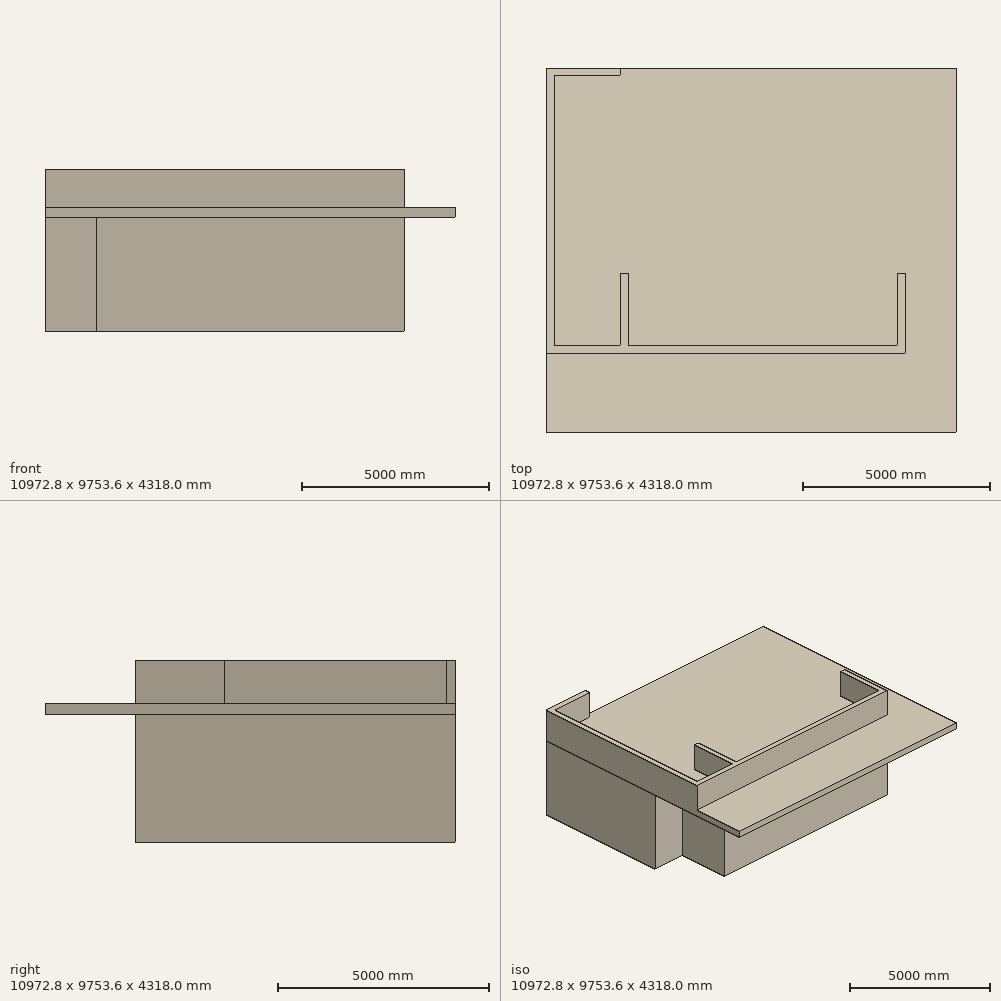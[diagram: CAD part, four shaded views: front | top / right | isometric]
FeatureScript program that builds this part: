
annotation { "Feature Type Name" : "Feature", "Feature Type Description" : "" }
export const myFeature = defineFeature(function(context is Context, id is Id, definition is map)
    precondition{}
    {
        {
            var Q0;
            Q0=qCreatedBy(makeId("Top.planeOp"),FACE);
            var sketch = newSketch(context, id + "F0", { "sketchPlane" : qUnion([Q0])});
            skLineSegment(sketch, "E0.bottom", {"start": v(-8229.6, 7620) * mm, "end": v(0, 7620) * mm});
            skLineSegment(sketch, "E0.top", {"start": v(-8229.6, 0) * mm, "end": v(0, 0) * mm});
            skLineSegment(sketch, "E0.left", {"start": v(-8229.6, 7620) * mm, "end": v(-8229.6, 0) * mm});
            skLineSegment(sketch, "E0.right", {"start": v(0, 7620) * mm, "end": v(0, 0) * mm});
            skLineSegment(sketch, "E1.bottom", {"start": v(-8077.2, 7467.6) * mm, "end": v(-152.4, 7467.6) * mm});
            skLineSegment(sketch, "E1.top", {"start": v(-8077.2, 152.4) * mm, "end": v(-152.4, 152.4) * mm});
            skLineSegment(sketch, "E1.left", {"start": v(-8077.2, 7467.6) * mm, "end": v(-8077.2, 152.4) * mm});
            skLineSegment(sketch, "E1.right", {"start": v(-152.4, 7467.6) * mm, "end": v(-152.4, 152.4) * mm});
            skSolve(sketch);
        }
        {
            var Q0;
            Q0 = qSketchRegion(id + "F0", true);
            extrude(context, id + "F1", {"entities" : qUnion([Q0]), "depth" : 3048 * mm});
        }
        {
            var Q0;
            Q0=qCreatedBy(makeId("Top.planeOp"),FACE);
            var sketch = newSketch(context, id + "F2", { "sketchPlane" : qUnion([Q0])});
            skLineSegment(sketch, "E2.bottom", {"start": v(-2934.46, 3909.43) * mm, "end": v(-1410.46, 3909.43) * mm});
            skLineSegment(sketch, "E2.top", {"start": v(-2934.46, 1166.23) * mm, "end": v(-1410.46, 1166.23) * mm});
            skLineSegment(sketch, "E2.left", {"start": v(-2934.46, 3909.43) * mm, "end": v(-2934.46, 1166.23) * mm});
            skLineSegment(sketch, "E2.right", {"start": v(-1410.46, 3909.43) * mm, "end": v(-1410.46, 1166.23) * mm});
            skSolve(sketch);
        }
        {
            var Q0;
            Q0 = qSketchRegion(id + "F2", true);
            extrude(context, id + "F3", {"entities" : qUnion([Q0]), "depth" : 1219.2 * mm});
        }
        {
            var Q0;
            Q0=qCreatedBy(makeId("Top.planeOp"),FACE);
            var sketch = newSketch(context, id + "F4", { "sketchPlane" : qUnion([Q0])});
            skLineSegment(sketch, "E3", {"start": v(-7377.5, 3939.47) * mm, "end": v(-5345.5, 3939.47) * mm});
            skLineSegment(sketch, "E4", {"start": v(-5345.5, 3939.47) * mm, "end": v(-5345.5, 637.47) * mm});
            skLineSegment(sketch, "E5", {"start": v(-5345.5, 637.47) * mm, "end": v(-7377.5, 637.47) * mm});
            skLineSegment(sketch, "E6", {"start": v(-6158.3, 3126.67) * mm, "end": v(-7377.5, 3126.67) * mm});
            skLineSegment(sketch, "E7", {"start": v(-7377.5, 3126.67) * mm, "end": v(-7377.5, 3939.47) * mm});
            skLineSegment(sketch, "E8", {"start": v(-6158.3, 3126.67) * mm, "end": v(-6158.3, 1450.27) * mm});
            skLineSegment(sketch, "E9", {"start": v(-6158.3, 1450.27) * mm, "end": v(-7377.5, 1450.27) * mm});
            skLineSegment(sketch, "E10", {"start": v(-7377.5, 1450.27) * mm, "end": v(-7377.5, 637.47) * mm});
            skSolve(sketch);
        }
        {
            var Q0;
            Q0 = qSketchRegion(id + "F4", true);
            extrude(context, id + "F5", {"entities" : qUnion([Q0]), "depth" : 914.4 * mm});
        }
        {
            var Q0;
            Q0=qCreatedBy(makeId("Top.planeOp"),FACE);
            var sketch = newSketch(context, id + "F6", { "sketchPlane" : qUnion([Q0])});
            skLineSegment(sketch, "E11.bottom", {"start": v(-8229.6, 7620) * mm, "end": v(-9601.2, 7620) * mm});
            skLineSegment(sketch, "E11.top", {"start": v(-8229.6, 2133.6) * mm, "end": v(-9601.2, 2133.6) * mm});
            skLineSegment(sketch, "E11.right", {"start": v(-9601.2, 7620) * mm, "end": v(-9601.2, 2133.6) * mm});
            skLineSegment(sketch, "E12.bottom", {"start": v(-9448.8, 7467.6) * mm, "end": v(-8229.6, 7467.6) * mm});
            skLineSegment(sketch, "E12.top", {"start": v(-9448.8, 2286) * mm, "end": v(-8229.6, 2286) * mm});
            skLineSegment(sketch, "E12.left", {"start": v(-9448.8, 7467.6) * mm, "end": v(-9448.8, 2286) * mm});
            skLineSegment(sketch, "E13", {"start": v(-8229.6, 7620) * mm, "end": v(-8229.6, 7467.6) * mm});
            skLineSegment(sketch, "E14", {"start": v(-8229.6, 2286) * mm, "end": v(-8229.6, 2133.6) * mm});
            skSolve(sketch);
        }
        {
            var Q0;
            Q0 = qSketchRegion(id + "F6", true);
            extrude(context, id + "F7", {"entities" : qUnion([Q0]), "operationType" : NewBodyOperationType.ADD, "depth" : 3048 * mm});
        }
        {
            var Q0;
            Q0=makeQuery(id+"F1.opExtrude","SWEPT_FACE",FACE,{"disambiguationData":[OSD([sQuery(id+"F0.wireOp",EDGE,"E1.left")])]});
            var sketch = newSketch(context, id + "F8", { "sketchPlane" : qUnion([Q0])});
            skLineSegment(sketch, "E15.bottom", {"start": v(2286, 0) * mm, "end": v(7467.6, 0) * mm});
            skLineSegment(sketch, "E15.top", {"start": v(2286, 3048) * mm, "end": v(7467.6, 3048) * mm});
            skLineSegment(sketch, "E15.left", {"start": v(2286, 0) * mm, "end": v(2286, 3048) * mm});
            skLineSegment(sketch, "E15.right", {"start": v(7467.6, 0) * mm, "end": v(7467.6, 3048) * mm});
            skSolve(sketch);
        }
        {
            var Q0;
            Q0 = qSketchRegion(id + "F8", true);
            extrude(context, id + "F9", {"entities" : qUnion([Q0]), "operationType" : NewBodyOperationType.REMOVE, "endBound" : BoundingType.UP_TO_NEXT, "oppositeDirection" : true, "depth" : 25.4 * mm});
        }
        {
            var Q0;
            Q0=makeQuery(id+"F7.boolean.opBoolean","MERGE",FACE,{"derivedFrom":[makeQuery(id+"F1.opExtrude","CAP_FACE",FACE,{"disambiguationData":[OSD([sQuery(id+"F0.wireOp",EDGE,"E0.bottom"),sQuery(id+"F0.wireOp",EDGE,"E0.top"),sQuery(id+"F0.wireOp",EDGE,"E0.left"),sQuery(id+"F0.wireOp",EDGE,"E0.right"),sQuery(id+"F0.wireOp",EDGE,"E1.bottom"),sQuery(id+"F0.wireOp",EDGE,"E1.top"),sQuery(id+"F0.wireOp",EDGE,"E1.left"),sQuery(id+"F0.wireOp",EDGE,"E1.right")])],"isStart":false}),makeQuery(id+"F7.opExtrude","CAP_FACE",FACE,{"disambiguationData":[OSD([sQuery(id+"F6.wireOp",EDGE,"E11.bottom"),sQuery(id+"F6.wireOp",EDGE,"E11.top"),sQuery(id+"F6.wireOp",EDGE,"E11.right"),sQuery(id+"F6.wireOp",EDGE,"E12.bottom"),sQuery(id+"F6.wireOp",EDGE,"E12.top"),sQuery(id+"F6.wireOp",EDGE,"E12.left"),sQuery(id+"F6.wireOp",EDGE,"E13"),sQuery(id+"F6.wireOp",EDGE,"E14")])],"isStart":false})]});
            var sketch = newSketch(context, id + "F10", { "sketchPlane" : qUnion([Q0])});
            skLineSegment(sketch, "E16", {"start": v(-6248.4, 7467.6) * mm, "end": v(-6248.4, 6502.4) * mm});
            skLineSegment(sketch, "E17", {"start": v(-6248.4, 6502.4) * mm, "end": v(-9448.8, 6502.4) * mm});
            skLineSegment(sketch, "E18", {"start": v(-9448.8, 6654.8) * mm, "end": v(-6400.8, 6654.8) * mm});
            skLineSegment(sketch, "E19", {"start": v(-6400.8, 6654.8) * mm, "end": v(-6400.8, 7467.6) * mm});
            skLineSegment(sketch, "E20", {"start": v(-6400.8, 7467.6) * mm, "end": v(-6248.4, 7467.6) * mm});
            skLineSegment(sketch, "E21", {"start": v(-9448.8, 6654.8) * mm, "end": v(-9448.8, 6502.4) * mm});
            skSolve(sketch);
        }
        {
            var Q0;
            Q0 = qSketchRegion(id + "F10", true);
            var Q1;
            Q1=makeQuery(id+"F7.boolean.opBoolean","MERGE",FACE,{"derivedFrom":[makeQuery(id+"F1.opExtrude","CAP_FACE",FACE,{"disambiguationData":[OSD([sQuery(id+"F0.wireOp",EDGE,"E0.bottom"),sQuery(id+"F0.wireOp",EDGE,"E0.top"),sQuery(id+"F0.wireOp",EDGE,"E0.left"),sQuery(id+"F0.wireOp",EDGE,"E0.right"),sQuery(id+"F0.wireOp",EDGE,"E1.bottom"),sQuery(id+"F0.wireOp",EDGE,"E1.top"),sQuery(id+"F0.wireOp",EDGE,"E1.left"),sQuery(id+"F0.wireOp",EDGE,"E1.right")])],"isStart":true}),makeQuery(id+"F7.opExtrude","CAP_FACE",FACE,{"disambiguationData":[OSD([sQuery(id+"F6.wireOp",EDGE,"E11.bottom"),sQuery(id+"F6.wireOp",EDGE,"E11.top"),sQuery(id+"F6.wireOp",EDGE,"E11.right"),sQuery(id+"F6.wireOp",EDGE,"E12.bottom"),sQuery(id+"F6.wireOp",EDGE,"E12.top"),sQuery(id+"F6.wireOp",EDGE,"E12.left"),sQuery(id+"F6.wireOp",EDGE,"E13"),sQuery(id+"F6.wireOp",EDGE,"E14")])],"isStart":true})]});
            extrude(context, id + "F11", {"entities" : qUnion([Q0]), "operationType" : NewBodyOperationType.ADD, "endBound" : BoundingType.UP_TO_SURFACE, "oppositeDirection" : true, "endBoundEntityFace" : qUnion([Q1]), "depth" : 25.4 * mm});
        }
        {
            var Q0;
            {var subQ0=sQuery(id+"F6.wireOp",EDGE,"E14");var subQ1=sQuery(id+"F6.wireOp",EDGE,"E13");var subQ2=sQuery(id+"F6.wireOp",EDGE,"E12.left");var subQ3=sQuery(id+"F6.wireOp",EDGE,"E12.top");var subQ4=sQuery(id+"F6.wireOp",EDGE,"E12.bottom");var subQ5=sQuery(id+"F6.wireOp",EDGE,"E11.right");var subQ6=sQuery(id+"F6.wireOp",EDGE,"E11.top");var subQ7=sQuery(id+"F6.wireOp",EDGE,"E11.bottom");var subQ8=sQuery(id+"F0.wireOp",EDGE,"E1.right");var subQ9=sQuery(id+"F0.wireOp",EDGE,"E1.left");var subQ10=sQuery(id+"F0.wireOp",EDGE,"E1.top");var subQ11=sQuery(id+"F0.wireOp",EDGE,"E1.bottom");var subQ12=sQuery(id+"F0.wireOp",EDGE,"E0.right");var subQ13=sQuery(id+"F0.wireOp",EDGE,"E0.left");var subQ14=sQuery(id+"F0.wireOp",EDGE,"E0.top");var subQ15=sQuery(id+"F0.wireOp",EDGE,"E0.bottom");Q0=makeQuery(id+"F11.boolean.opBoolean","MERGE",FACE,{"derivedFrom":[makeQuery(id+"F7.boolean.opBoolean","MERGE",FACE,{"derivedFrom":[makeQuery(id+"F1.opExtrude","CAP_FACE",FACE,{"disambiguationData":[OSD([subQ15,subQ14,subQ13,subQ12,subQ11,subQ10,subQ9,subQ8])],"isStart":true}),makeQuery(id+"F7.opExtrude","CAP_FACE",FACE,{"disambiguationData":[OSD([subQ7,subQ6,subQ5,subQ4,subQ3,subQ2,subQ1,subQ0])],"isStart":true})]}),makeQuery(id+"F11.opExtrude","CAP_FACE",FACE,{"disambiguationData":[OSD([subQ15,subQ14,subQ13,subQ12,subQ11,subQ10,subQ9,subQ8,subQ7,subQ6,subQ5,subQ4,subQ3,subQ2,subQ1,subQ0])],"isStart":false})]});}
            var sketch = newSketch(context, id + "F12", { "sketchPlane" : qUnion([Q0])});
            skLineSegment(sketch, "E22", {"start": v(-6248.4, -6502.4) * mm, "end": v(-6248.4, -5283.2) * mm});
            skLineSegment(sketch, "E23", {"start": v(-6248.4, -5283.2) * mm, "end": v(-8077.2, -5283.2) * mm});
            skLineSegment(sketch, "E24", {"start": v(-8229.6, -5435.6) * mm, "end": v(-6400.8, -5435.6) * mm});
            skLineSegment(sketch, "E25", {"start": v(-6400.8, -5435.6) * mm, "end": v(-6400.8, -6502.4) * mm});
            skLineSegment(sketch, "E26", {"start": v(-6400.8, -6502.4) * mm, "end": v(-6248.4, -6502.4) * mm});
            skLineSegment(sketch, "E27", {"start": v(-8229.6, -5435.6) * mm, "end": v(-8229.6, -3505.2) * mm});
            skLineSegment(sketch, "E28", {"start": v(-8229.6, -3505.2) * mm, "end": v(-8077.2, -3505.2) * mm});
            skLineSegment(sketch, "E29", {"start": v(-8077.2, -3505.2) * mm, "end": v(-8077.2, -5283.2) * mm});
            skSolve(sketch);
        }
        {
            var Q0;
            Q0 = qSketchRegion(id + "F12", true);
            var Q1;
            Q1=makeQuery(id+"F11.boolean.opBoolean","MERGE",FACE,{"derivedFrom":[makeQuery(id+"F7.boolean.opBoolean","MERGE",FACE,{"derivedFrom":[makeQuery(id+"F1.opExtrude","CAP_FACE",FACE,{"disambiguationData":[OSD([sQuery(id+"F0.wireOp",EDGE,"E0.bottom"),sQuery(id+"F0.wireOp",EDGE,"E0.top"),sQuery(id+"F0.wireOp",EDGE,"E0.left"),sQuery(id+"F0.wireOp",EDGE,"E0.right"),sQuery(id+"F0.wireOp",EDGE,"E1.bottom"),sQuery(id+"F0.wireOp",EDGE,"E1.top"),sQuery(id+"F0.wireOp",EDGE,"E1.left"),sQuery(id+"F0.wireOp",EDGE,"E1.right")])],"isStart":false}),makeQuery(id+"F7.opExtrude","CAP_FACE",FACE,{"disambiguationData":[OSD([sQuery(id+"F6.wireOp",EDGE,"E11.bottom"),sQuery(id+"F6.wireOp",EDGE,"E11.top"),sQuery(id+"F6.wireOp",EDGE,"E11.right"),sQuery(id+"F6.wireOp",EDGE,"E12.bottom"),sQuery(id+"F6.wireOp",EDGE,"E12.top"),sQuery(id+"F6.wireOp",EDGE,"E12.left"),sQuery(id+"F6.wireOp",EDGE,"E13"),sQuery(id+"F6.wireOp",EDGE,"E14")])],"isStart":false})]}),makeQuery(id+"F11.opExtrude","CAP_FACE",FACE,{"disambiguationData":[OSD([sQuery(id+"F10.wireOp",EDGE,"E16"),sQuery(id+"F10.wireOp",EDGE,"E17"),sQuery(id+"F10.wireOp",EDGE,"E18"),sQuery(id+"F10.wireOp",EDGE,"E19"),sQuery(id+"F10.wireOp",EDGE,"E20"),sQuery(id+"F10.wireOp",EDGE,"E21")])],"isStart":true})]});
            extrude(context, id + "F13", {"entities" : qUnion([Q0]), "operationType" : NewBodyOperationType.ADD, "oppositeDirection" : true, "endBoundEntityFace" : qUnion([Q1]), "depth" : 914.4 * mm});
        }
        {
            var Q0;
            Q0=makeQuery(id+"F1.opExtrude","SWEPT_FACE",FACE,{"disambiguationData":[OSD([sQuery(id+"F0.wireOp",EDGE,"E0.right")])]});
            var sketch = newSketch(context, id + "F14", { "sketchPlane" : qUnion([Q0])});
            skLineSegment(sketch, "E30.bottom", {"start": v(0, 3048) * mm, "end": v(7620, 3048) * mm});
            skLineSegment(sketch, "E30.top", {"start": v(0, 0) * mm, "end": v(7620, 0) * mm});
            skLineSegment(sketch, "E30.left", {"start": v(0, 3048) * mm, "end": v(0, 0) * mm});
            skLineSegment(sketch, "E30.right", {"start": v(7620, 3048) * mm, "end": v(7620, 0) * mm});
            skSolve(sketch);
        }
        {
            var Q0;
            Q0=makeQuery(id+"F11.boolean.opBoolean","MERGE",FACE,{"derivedFrom":[makeQuery(id+"F7.boolean.opBoolean","MERGE",FACE,{"derivedFrom":[makeQuery(id+"F1.opExtrude","CAP_FACE",FACE,{"disambiguationData":[OSD([sQuery(id+"F0.wireOp",EDGE,"E0.bottom"),sQuery(id+"F0.wireOp",EDGE,"E0.top"),sQuery(id+"F0.wireOp",EDGE,"E0.left"),sQuery(id+"F0.wireOp",EDGE,"E0.right"),sQuery(id+"F0.wireOp",EDGE,"E1.bottom"),sQuery(id+"F0.wireOp",EDGE,"E1.top"),sQuery(id+"F0.wireOp",EDGE,"E1.left"),sQuery(id+"F0.wireOp",EDGE,"E1.right")])],"isStart":false}),makeQuery(id+"F7.opExtrude","CAP_FACE",FACE,{"disambiguationData":[OSD([sQuery(id+"F6.wireOp",EDGE,"E11.bottom"),sQuery(id+"F6.wireOp",EDGE,"E11.top"),sQuery(id+"F6.wireOp",EDGE,"E11.right"),sQuery(id+"F6.wireOp",EDGE,"E12.bottom"),sQuery(id+"F6.wireOp",EDGE,"E12.top"),sQuery(id+"F6.wireOp",EDGE,"E12.left"),sQuery(id+"F6.wireOp",EDGE,"E13"),sQuery(id+"F6.wireOp",EDGE,"E14")])],"isStart":false})]}),makeQuery(id+"F11.opExtrude","CAP_FACE",FACE,{"disambiguationData":[OSD([sQuery(id+"F10.wireOp",EDGE,"E16"),sQuery(id+"F10.wireOp",EDGE,"E17"),sQuery(id+"F10.wireOp",EDGE,"E18"),sQuery(id+"F10.wireOp",EDGE,"E19"),sQuery(id+"F10.wireOp",EDGE,"E20"),sQuery(id+"F10.wireOp",EDGE,"E21")])],"isStart":true})]});
            var sketch = newSketch(context, id + "F15", { "sketchPlane" : qUnion([Q0])});
            skLineSegment(sketch, "E31.bottom", {"start": v(-9601.2, 7620) * mm, "end": v(0, 7620) * mm});
            skLineSegment(sketch, "E31.top", {"start": v(-9601.2, 0) * mm, "end": v(0, 0) * mm});
            skLineSegment(sketch, "E31.left", {"start": v(-9601.2, 7620) * mm, "end": v(-9601.2, 0) * mm});
            skLineSegment(sketch, "E31.right", {"start": v(0, 7620) * mm, "end": v(0, 0) * mm});
            skSolve(sketch);
        }
        {
            var Q0;
            Q0 = qSketchRegion(id + "F15", true);
            extrude(context, id + "F16", {"entities" : qUnion([Q0]), "depth" : 254 * mm});
        }
        {
            var Q0;
            Q0=makeQuery(id+"F16.opExtrude","CAP_FACE",FACE,{"disambiguationData":[OSD([sQuery(id+"F15.wireOp",EDGE,"E31.bottom"),sQuery(id+"F15.wireOp",EDGE,"E31.top"),sQuery(id+"F15.wireOp",EDGE,"E31.left"),sQuery(id+"F15.wireOp",EDGE,"E31.right")])],"isStart":false});
            var sketch = newSketch(context, id + "F17", { "sketchPlane" : qUnion([Q0])});
            skLineSegment(sketch, "E32", {"start": v(0, 2133.6) * mm, "end": v(0, 0) * mm});
            skLineSegment(sketch, "E33", {"start": v(0, 0) * mm, "end": v(-9601.2, 0) * mm});
            skLineSegment(sketch, "E34", {"start": v(-9601.2, 0) * mm, "end": v(-9601.2, 7620) * mm});
            skLineSegment(sketch, "E35", {"start": v(-9601.2, 7620) * mm, "end": v(-7620, 7620) * mm});
            skLineSegment(sketch, "E36", {"start": v(-7620, 7620) * mm, "end": v(-7620, 7416.8) * mm});
            skLineSegment(sketch, "E37", {"start": v(-7620, 7416.8) * mm, "end": v(-9398, 7416.8) * mm});
            skLineSegment(sketch, "E38", {"start": v(-9398, 7416.8) * mm, "end": v(-9398, 203.2) * mm});
            skLineSegment(sketch, "E39", {"start": v(-9398, 203.2) * mm, "end": v(-203.2, 203.2) * mm});
            skLineSegment(sketch, "E40", {"start": v(-203.2, 203.2) * mm, "end": v(-203.2, 2133.6) * mm});
            skLineSegment(sketch, "E41", {"start": v(-203.2, 2133.6) * mm, "end": v(0, 2133.6) * mm});
            skSolve(sketch);
        }
        {
            var Q0;
            Q0 = qSketchRegion(id + "F17", true);
            extrude(context, id + "F18", {"entities" : qUnion([Q0]), "operationType" : NewBodyOperationType.ADD, "depth" : 1016 * mm});
        }
        {
            var Q0;
            Q0=makeQuery(id+"F11.boolean.opBoolean","MERGE",FACE,{"derivedFrom":[makeQuery(id+"F7.boolean.opBoolean","MERGE",FACE,{"derivedFrom":[makeQuery(id+"F1.opExtrude","CAP_FACE",FACE,{"disambiguationData":[OSD([sQuery(id+"F0.wireOp",EDGE,"E0.bottom"),sQuery(id+"F0.wireOp",EDGE,"E0.top"),sQuery(id+"F0.wireOp",EDGE,"E0.left"),sQuery(id+"F0.wireOp",EDGE,"E0.right"),sQuery(id+"F0.wireOp",EDGE,"E1.bottom"),sQuery(id+"F0.wireOp",EDGE,"E1.top"),sQuery(id+"F0.wireOp",EDGE,"E1.left"),sQuery(id+"F0.wireOp",EDGE,"E1.right")])],"isStart":false}),makeQuery(id+"F7.opExtrude","CAP_FACE",FACE,{"disambiguationData":[OSD([sQuery(id+"F6.wireOp",EDGE,"E11.bottom"),sQuery(id+"F6.wireOp",EDGE,"E11.top"),sQuery(id+"F6.wireOp",EDGE,"E11.right"),sQuery(id+"F6.wireOp",EDGE,"E12.bottom"),sQuery(id+"F6.wireOp",EDGE,"E12.top"),sQuery(id+"F6.wireOp",EDGE,"E12.left"),sQuery(id+"F6.wireOp",EDGE,"E13"),sQuery(id+"F6.wireOp",EDGE,"E14")])],"isStart":false})]}),makeQuery(id+"F11.opExtrude","CAP_FACE",FACE,{"disambiguationData":[OSD([sQuery(id+"F10.wireOp",EDGE,"E16"),sQuery(id+"F10.wireOp",EDGE,"E17"),sQuery(id+"F10.wireOp",EDGE,"E18"),sQuery(id+"F10.wireOp",EDGE,"E19"),sQuery(id+"F10.wireOp",EDGE,"E20"),sQuery(id+"F10.wireOp",EDGE,"E21")])],"isStart":true})]});
            var sketch = newSketch(context, id + "F19", { "sketchPlane" : qUnion([Q0])});
            skLineSegment(sketch, "E42.bottom", {"start": v(-9601.2, 7620) * mm, "end": v(1371.6, 7620) * mm});
            skLineSegment(sketch, "E42.top", {"start": v(-9601.2, -2133.6) * mm, "end": v(1371.6, -2133.6) * mm});
            skLineSegment(sketch, "E42.left", {"start": v(-9601.2, 7620) * mm, "end": v(-9601.2, -2133.6) * mm});
            skLineSegment(sketch, "E42.right", {"start": v(1371.6, 7620) * mm, "end": v(1371.6, -2133.6) * mm});
            skSolve(sketch);
        }
        {
            var Q0;
            Q0 = qSketchRegion(id + "F19", true);
            extrude(context, id + "F20", {"entities" : qUnion([Q0]), "depth" : 254 * mm});
        }
        {
            var Q0;
            Q0=makeQuery(id+"F11.boolean.opBoolean","MERGE",FACE,{"derivedFrom":[makeQuery(id+"F7.boolean.opBoolean","MERGE",FACE,{"derivedFrom":[makeQuery(id+"F1.opExtrude","CAP_FACE",FACE,{"disambiguationData":[OSD([sQuery(id+"F0.wireOp",EDGE,"E0.bottom"),sQuery(id+"F0.wireOp",EDGE,"E0.top"),sQuery(id+"F0.wireOp",EDGE,"E0.left"),sQuery(id+"F0.wireOp",EDGE,"E0.right"),sQuery(id+"F0.wireOp",EDGE,"E1.bottom"),sQuery(id+"F0.wireOp",EDGE,"E1.top"),sQuery(id+"F0.wireOp",EDGE,"E1.left"),sQuery(id+"F0.wireOp",EDGE,"E1.right")])],"isStart":false}),makeQuery(id+"F7.opExtrude","CAP_FACE",FACE,{"disambiguationData":[OSD([sQuery(id+"F6.wireOp",EDGE,"E11.bottom"),sQuery(id+"F6.wireOp",EDGE,"E11.top"),sQuery(id+"F6.wireOp",EDGE,"E11.right"),sQuery(id+"F6.wireOp",EDGE,"E12.bottom"),sQuery(id+"F6.wireOp",EDGE,"E12.top"),sQuery(id+"F6.wireOp",EDGE,"E12.left"),sQuery(id+"F6.wireOp",EDGE,"E13"),sQuery(id+"F6.wireOp",EDGE,"E14")])],"isStart":false})]}),makeQuery(id+"F11.opExtrude","CAP_FACE",FACE,{"disambiguationData":[OSD([sQuery(id+"F10.wireOp",EDGE,"E16"),sQuery(id+"F10.wireOp",EDGE,"E17"),sQuery(id+"F10.wireOp",EDGE,"E18"),sQuery(id+"F10.wireOp",EDGE,"E19"),sQuery(id+"F10.wireOp",EDGE,"E20"),sQuery(id+"F10.wireOp",EDGE,"E21")])],"isStart":true})]});
            var sketch = newSketch(context, id + "F21", { "sketchPlane" : qUnion([Q0])});
            skLineSegment(sketch, "E43.bottom", {"start": v(-9601.2, 7620) * mm, "end": v(0, 7620) * mm});
            skLineSegment(sketch, "E43.top", {"start": v(-9601.2, 0) * mm, "end": v(0, 0) * mm});
            skLineSegment(sketch, "E43.left", {"start": v(-9601.2, 7620) * mm, "end": v(-9601.2, 0) * mm});
            skLineSegment(sketch, "E43.right", {"start": v(0, 7620) * mm, "end": v(0, 0) * mm});
            skSolve(sketch);
        }
        {
            var Q0;
            Q0 = qSketchRegion(id + "F21", true);
            extrude(context, id + "F22", {"entities" : qUnion([Q0]), "depth" : 254 * mm});
        }
        {
            var Q0;
            Q0=makeQuery(id+"F22.opExtrude","CAP_FACE",FACE,{"disambiguationData":[OSD([sQuery(id+"F21.wireOp",EDGE,"E43.bottom"),sQuery(id+"F21.wireOp",EDGE,"E43.top"),sQuery(id+"F21.wireOp",EDGE,"E43.left"),sQuery(id+"F21.wireOp",EDGE,"E43.right")])],"isStart":false});
            var sketch = newSketch(context, id + "F23", { "sketchPlane" : qUnion([Q0])});
            skLineSegment(sketch, "E44", {"start": v(0, 2133.6) * mm, "end": v(0, 0) * mm});
            skLineSegment(sketch, "E45", {"start": v(0, 0) * mm, "end": v(-7620, 0) * mm});
            skLineSegment(sketch, "E46", {"start": v(-7620, 0) * mm, "end": v(-7620, 2133.6) * mm});
            skLineSegment(sketch, "E47", {"start": v(-7620, 2133.6) * mm, "end": v(-7416.8, 2133.6) * mm});
            skLineSegment(sketch, "E48", {"start": v(-7416.8, 2133.6) * mm, "end": v(-7416.8, 203.2) * mm});
            skLineSegment(sketch, "E49", {"start": v(-7416.8, 203.2) * mm, "end": v(-203.2, 203.2) * mm});
            skLineSegment(sketch, "E50", {"start": v(-203.2, 203.2) * mm, "end": v(-203.2, 2133.6) * mm});
            skLineSegment(sketch, "E51", {"start": v(-203.2, 2133.6) * mm, "end": v(0, 2133.6) * mm});
            skSolve(sketch);
        }
        {
            var Q0;
            Q0 = qSketchRegion(id + "F23", true);
            extrude(context, id + "F24", {"entities" : qUnion([Q0]), "operationType" : NewBodyOperationType.ADD, "depth" : 1016 * mm});
        }
    });
